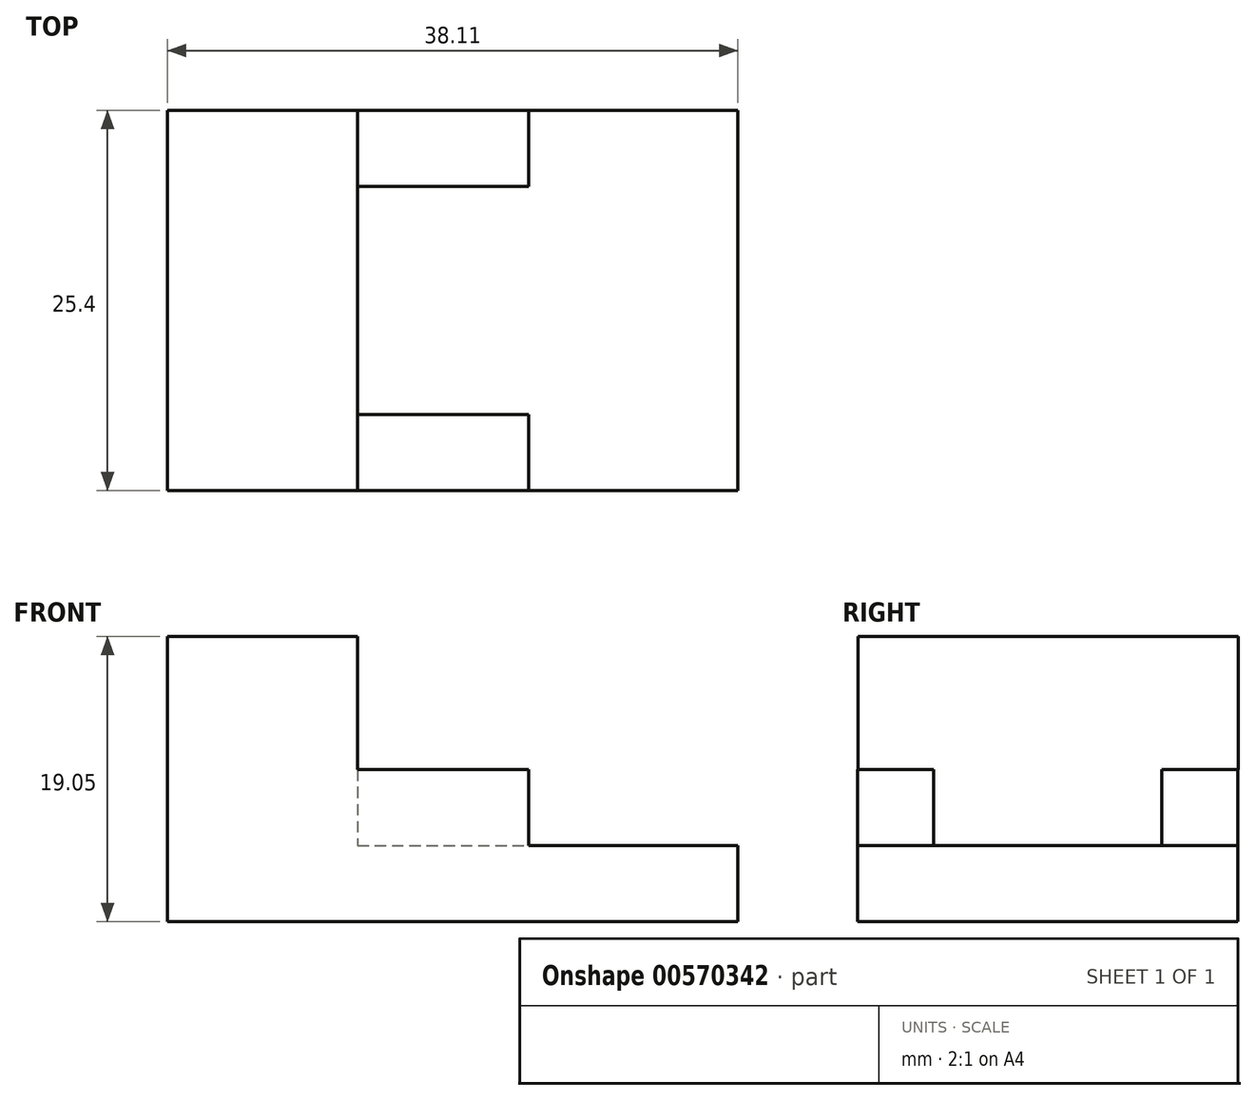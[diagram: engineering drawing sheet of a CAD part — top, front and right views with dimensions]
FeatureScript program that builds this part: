
annotation { "Feature Type Name" : "Feature", "Feature Type Description" : "" }
export const myFeature = defineFeature(function(context is Context, id is Id, definition is map)
    precondition{}
    {
        {
            var Q0;
            Q0=qCreatedBy(makeId("Top.planeOp"),FACE);
            var sketch = newSketch(context, id + "F0", { "sketchPlane" : qUnion([Q0])});
            skLineSegment(sketch, "E0.bottom", {"start": v(-19.05, 12.7) * mm, "end": v(19.05, 12.7) * mm});
            skLineSegment(sketch, "E0.top", {"start": v(-19.05, -12.7) * mm, "end": v(19.05, -12.7) * mm});
            skLineSegment(sketch, "E0.left", {"start": v(-19.05, 12.7) * mm, "end": v(-19.05, -12.7) * mm});
            skLineSegment(sketch, "E0.right", {"start": v(19.05, 12.7) * mm, "end": v(19.05, -12.7) * mm});
            skPoint(sketch, "E0.middle", {"position": v(0, 0) * mm});
            skSolve(sketch);
        }
        {
            var Q0;
            Q0=makeQuery(id+"F0.imprint","IMPRINT",FACE,{"disambiguationData":[TD([[makeQuery(id+"F0.imprint","IMPRINT",EDGE,{"derivedFrom":sQuery(id+"F0.wireOp",EDGE,"E0.bottom")}),-1.0]])]});
            var sketch = newSketch(context, id + "F1", { "sketchPlane" : qUnion([Q0])});
            skLineSegment(sketch, "E1.bottom", {"start": v(-19.06, -12.7) * mm, "end": v(-6.36, -12.7) * mm});
            skLineSegment(sketch, "E1.top", {"start": v(-19.06, 12.7) * mm, "end": v(-6.36, 12.7) * mm});
            skLineSegment(sketch, "E1.left", {"start": v(-19.06, -12.7) * mm, "end": v(-19.06, 12.7) * mm});
            skLineSegment(sketch, "E1.right", {"start": v(-6.36, -12.7) * mm, "end": v(-6.36, 12.7) * mm});
            skSolve(sketch);
        }
        {
            var Q0;
            Q0 = qSketchRegion(id + "F1", true);
            extrude(context, id + "F2", {"entities" : qUnion([Q0]), "depth" : 19.05 * mm, "offsetDistance" : 25.4 * mm});
        }
        {
            var Q0;
            Q0=makeQuery(id+"F0.imprint","IMPRINT",FACE,{"disambiguationData":[TD([[makeQuery(id+"F0.imprint","IMPRINT",EDGE,{"derivedFrom":sQuery(id+"F0.wireOp",EDGE,"E0.bottom")}),-1.0]])]});
            extrude(context, id + "F3", {"entities" : qUnion([Q0]), "operationType" : NewBodyOperationType.ADD, "depth" : 5.08 * mm, "offsetDistance" : 25.4 * mm});
        }
        {
            var Q0;
            Q0=makeQuery(id+"F3.opExtrude","CAP_FACE",FACE,{"disambiguationData":[OSD([sQuery(id+"F0.wireOp",EDGE,"E0.bottom"),sQuery(id+"F0.wireOp",EDGE,"E0.top"),sQuery(id+"F0.wireOp",EDGE,"E0.left"),sQuery(id+"F0.wireOp",EDGE,"E0.right")])],"isStart":false});
            var sketch = newSketch(context, id + "F4", { "sketchPlane" : qUnion([Q0])});
            skLineSegment(sketch, "E2.bottom", {"start": v(-6.36, -12.7) * mm, "end": v(5.07, -12.7) * mm});
            skLineSegment(sketch, "E2.top", {"start": v(-6.36, -7.62) * mm, "end": v(5.07, -7.62) * mm});
            skLineSegment(sketch, "E2.left", {"start": v(-6.36, -12.7) * mm, "end": v(-6.36, -7.62) * mm});
            skLineSegment(sketch, "E2.right", {"start": v(5.07, -12.7) * mm, "end": v(5.07, -7.62) * mm});
            skLineSegment(sketch, "E3.bottom", {"start": v(-6.36, 12.7) * mm, "end": v(5.07, 12.7) * mm});
            skLineSegment(sketch, "E3.top", {"start": v(-6.36, 7.62) * mm, "end": v(5.07, 7.62) * mm});
            skLineSegment(sketch, "E3.left", {"start": v(-6.36, 12.7) * mm, "end": v(-6.36, 7.62) * mm});
            skLineSegment(sketch, "E3.right", {"start": v(5.07, 12.7) * mm, "end": v(5.07, 7.62) * mm});
            skSolve(sketch);
        }
        {
            var Q0;
            Q0 = qSketchRegion(id + "F4", true);
            var Q1;
            Q1=makeQuery(id+"F4.imprint","IMPRINT",FACE,{"disambiguationData":[TD([[makeQuery(id+"F4.imprint","IMPRINT",EDGE,{"derivedFrom":sQuery(id+"F4.wireOp",EDGE,"E2.bottom")}),1.0]])]});
            var Q2;
            Q2=makeQuery(id+"F4.imprint","IMPRINT",FACE,{"disambiguationData":[TD([[makeQuery(id+"F4.imprint","IMPRINT",EDGE,{"derivedFrom":sQuery(id+"F4.wireOp",EDGE,"E3.bottom")}),1.0]])]});
            extrude(context, id + "F5", {"entities" : qUnion([Q0, Q1, Q2]), "operationType" : NewBodyOperationType.ADD, "depth" : 5.08 * mm, "offsetDistance" : 25.4 * mm});
        }
    });
